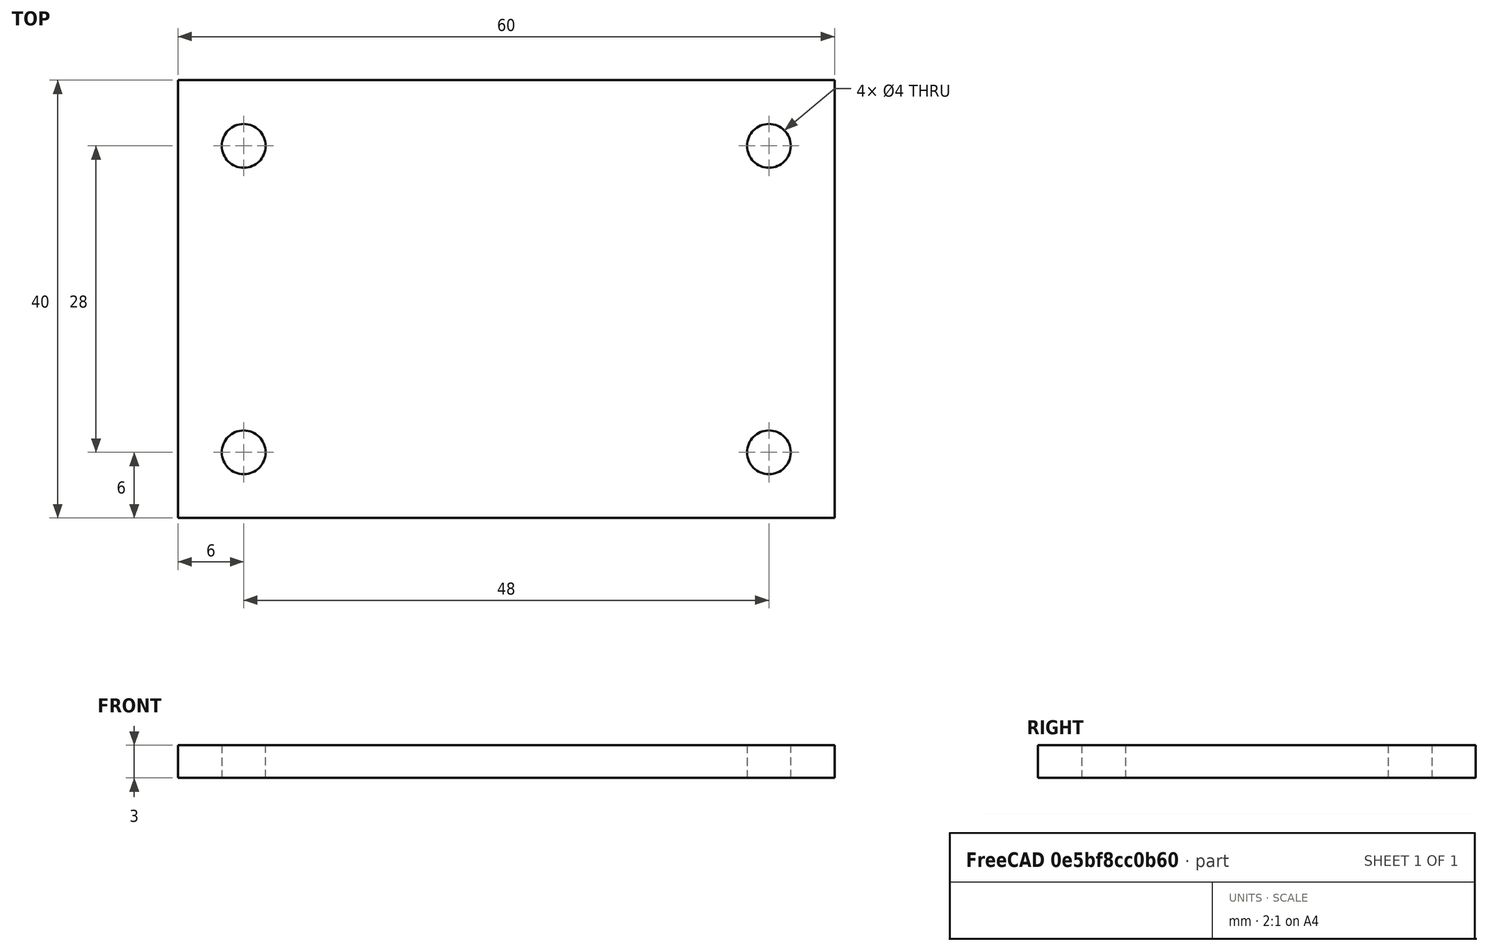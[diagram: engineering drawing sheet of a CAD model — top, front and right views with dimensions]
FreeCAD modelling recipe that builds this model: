
FCSTD DOCUMENT  (FreeCAD 0.21R33694 (Git))
Label: OJT1_T19P01_restriccions_simetria
License: All rights reserved
LicenseURL: https://en.wikipedia.org/wiki/All_rights_reserved
objects: Sketcher::SketchObject×1, PartDesign::Pad×1, PartDesign::Body×1
note: 4 computed .brp shape members not serialized (recipe doc carries the construction recipe); baked Part::Feature solids carry a one-line shape summary decoded from their .brp

FEATURE [Sketcher::SketchObject] Sketch
  FullyConstrained = true
  MapMode = 5
  Support = -> [XY_Plane]
  sketch-geometry (8):
    g0: LineSegment StartX=-30 StartY=20 StartZ=0 EndX=30 EndY=20 EndZ=0
    g1: LineSegment StartX=30 StartY=20 StartZ=0 EndX=30 EndY=-20 EndZ=0
    g2: LineSegment StartX=30 StartY=-20 StartZ=0 EndX=-30 EndY=-20 EndZ=0
    g3: LineSegment StartX=-30 StartY=-20 StartZ=0 EndX=-30 EndY=20 EndZ=0
    g4: Circle CenterX=-24 CenterY=14 CenterZ=0 NormalX=0 NormalY=0 NormalZ=1 AngleXU=0 Radius=2
    g5: Circle CenterX=-24 CenterY=-14 CenterZ=0 NormalX=0 NormalY=0 NormalZ=1 AngleXU=0 Radius=2
    g6: Circle CenterX=24 CenterY=-14 CenterZ=0 NormalX=0 NormalY=0 NormalZ=1 AngleXU=0 Radius=2
    g7: Circle CenterX=24 CenterY=14 CenterZ=0 NormalX=0 NormalY=0 NormalZ=1 AngleXU=0 Radius=2
  constraints (19):
    c: Coincident(g0,g1)
    c: Coincident(g1,g2)
    c: Coincident(g2,g3)
    c: Coincident(g3,g0)
    c: Horizontal(g2)
    c: Vertical(g1)
    c: Symmetric(g0,g0,g-2)
    c: Symmetric(g2,g0,g-1)
    c: Equal(g4,g5)
    c: Equal(g5,g6)
    c: Equal(g6,g7)
    c: Symmetric(g4,g7,g-2)
    c: Symmetric(g5,g6,g-2)
    c: Symmetric(g4,g5,g-1)
    c: DistanceX(g0,g4) = 6
    c: DistanceY(g4,g0) = 6
    c: Radius(g4) = 2
    c: DistanceX(g2,g2) = 60
    c: DistanceY(g1,g1) = 40
FEATURE [PartDesign::Pad] Pad
  Direction = (0,0,1)
  Length = 3
  Length2 = 10
  Profile = -> Sketch
  ReferenceAxis = -> Sketch [N_Axis]
  Type = 0
FEATURE [PartDesign::Body] Body
  Group = -> [Sketch,Pad]
  Origin = -> Origin
  Tip = -> Pad
